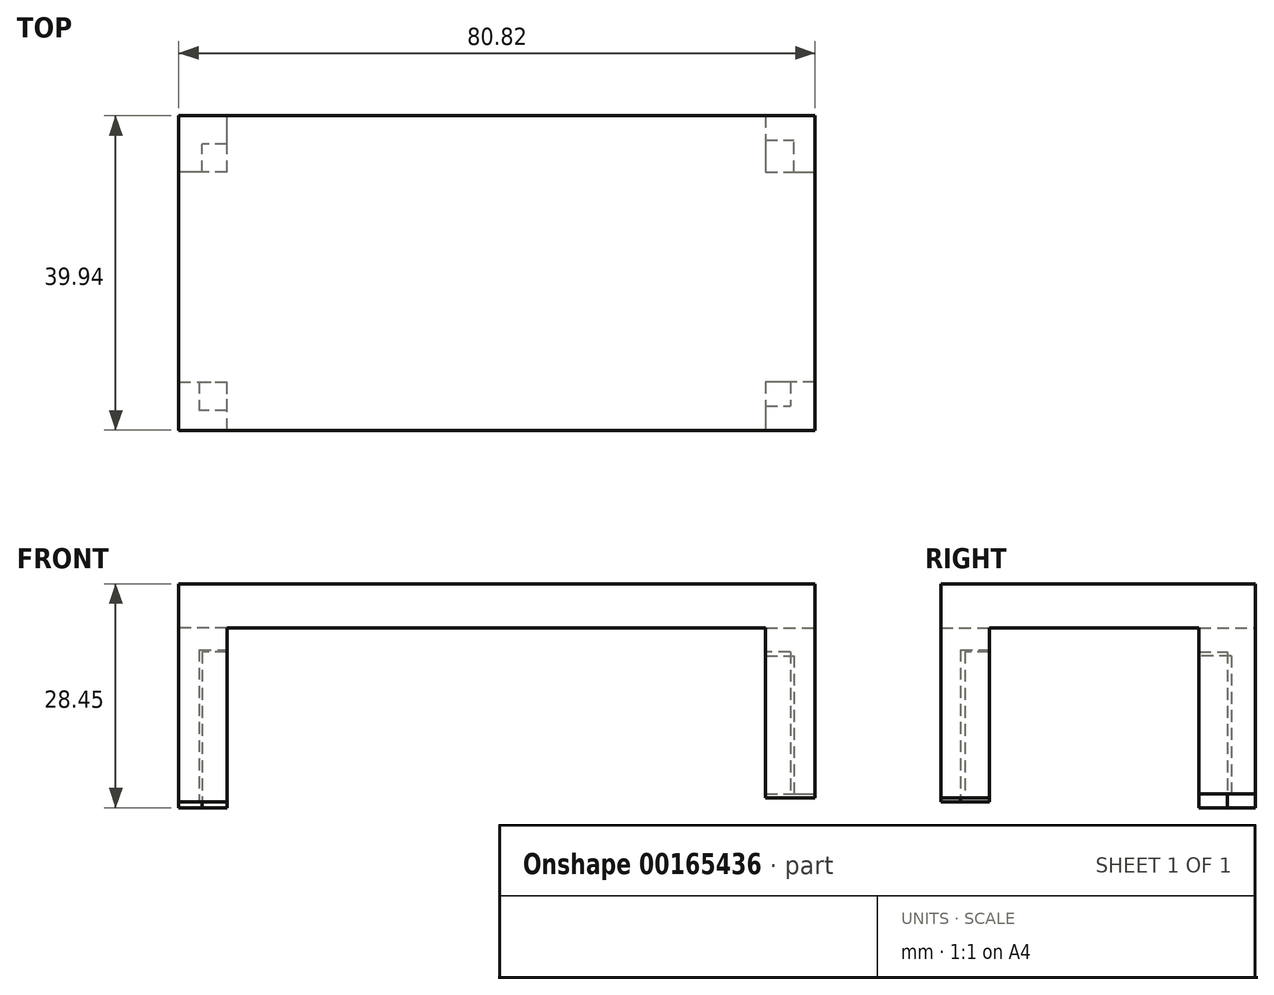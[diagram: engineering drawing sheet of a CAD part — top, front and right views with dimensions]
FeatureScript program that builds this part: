
annotation { "Feature Type Name" : "Feature", "Feature Type Description" : "" }
export const myFeature = defineFeature(function(context is Context, id is Id, definition is map)
    precondition{}
    {
        {
            var Q0;
            Q0=qCreatedBy(makeId("Top.planeOp"),FACE);
            var sketch = newSketch(context, id + "F0", { "sketchPlane" : qUnion([Q0])});
            skLineSegment(sketch, "E0.bottom", {"start": v(-43.18, 17.66) * mm, "end": v(37.64, 17.66) * mm});
            skLineSegment(sketch, "E0.top", {"start": v(-43.18, -22.28) * mm, "end": v(37.64, -22.28) * mm});
            skLineSegment(sketch, "E0.left", {"start": v(-43.18, 17.66) * mm, "end": v(-43.18, -22.28) * mm});
            skLineSegment(sketch, "E0.right", {"start": v(37.64, 17.66) * mm, "end": v(37.64, -22.28) * mm});
            skSolve(sketch);
        }
        {
            var Q0;
            Q0=makeQuery(id+"F0.imprint","IMPRINT",FACE,{"disambiguationData":[TD([[makeQuery(id+"F0.imprint","IMPRINT",EDGE,{"derivedFrom":sQuery(id+"F0.wireOp",EDGE,"E0.bottom")}),-1.0]])]});
            extrude(context, id + "F1", {"entities" : qUnion([Q0]), "depth" : 5.6 * mm});
        }
        {
            var Q0;
            Q0=makeQuery(id+"F1.opExtrude","CAP_FACE",FACE,{"disambiguationData":[OSD([sQuery(id+"F0.wireOp",EDGE,"E0.bottom"),sQuery(id+"F0.wireOp",EDGE,"E0.top"),sQuery(id+"F0.wireOp",EDGE,"E0.left"),sQuery(id+"F0.wireOp",EDGE,"E0.right")])],"isStart":true});
            var sketch = newSketch(context, id + "F2", { "sketchPlane" : qUnion([Q0])});
            skLineSegment(sketch, "E1.bottom", {"start": v(-43.18, 22.28) * mm, "end": v(-37.04, 22.28) * mm});
            skLineSegment(sketch, "E1.top", {"start": v(-43.18, 16.14) * mm, "end": v(-37.04, 16.14) * mm});
            skLineSegment(sketch, "E1.left", {"start": v(-43.18, 22.28) * mm, "end": v(-43.18, 16.14) * mm});
            skLineSegment(sketch, "E1.right", {"start": v(-37.04, 22.28) * mm, "end": v(-37.04, 16.14) * mm});
            skLineSegment(sketch, "E2.bottom", {"start": v(37.64, 16.14) * mm, "end": v(31.35, 16.14) * mm});
            skLineSegment(sketch, "E2.top", {"start": v(37.64, 22.28) * mm, "end": v(31.35, 22.28) * mm});
            skLineSegment(sketch, "E2.left", {"start": v(37.64, 16.14) * mm, "end": v(37.64, 22.28) * mm});
            skLineSegment(sketch, "E2.right", {"start": v(31.35, 16.14) * mm, "end": v(31.35, 22.28) * mm});
            skLineSegment(sketch, "E3.bottom", {"start": v(31.35, -17.66) * mm, "end": v(37.64, -17.66) * mm});
            skLineSegment(sketch, "E3.top", {"start": v(31.35, -10.5) * mm, "end": v(37.64, -10.5) * mm});
            skLineSegment(sketch, "E3.left", {"start": v(31.35, -17.66) * mm, "end": v(31.35, -10.5) * mm});
            skLineSegment(sketch, "E3.right", {"start": v(37.64, -17.66) * mm, "end": v(37.64, -10.5) * mm});
            skLineSegment(sketch, "E4.bottom", {"start": v(-37.04, -10.5) * mm, "end": v(-43.18, -10.5) * mm});
            skLineSegment(sketch, "E4.top", {"start": v(-37.04, -17.66) * mm, "end": v(-43.18, -17.66) * mm});
            skLineSegment(sketch, "E4.left", {"start": v(-37.04, -10.5) * mm, "end": v(-37.04, -17.66) * mm});
            skLineSegment(sketch, "E4.right", {"start": v(-43.18, -10.5) * mm, "end": v(-43.18, -17.66) * mm});
            skSolve(sketch);
        }
        {
            var Q0;
            Q0=makeQuery(id+"F2.imprint","IMPRINT",FACE,{"disambiguationData":[TD([[makeQuery(id+"F2.imprint","IMPRINT",EDGE,{"derivedFrom":sQuery(id+"F2.wireOp",EDGE,"E1.bottom")}),-1.0]])]});
            extrude(context, id + "F3", {"entities" : qUnion([Q0]), "operationType" : NewBodyOperationType.ADD, "depth" : 22.1 * mm});
        }
        {
            var Q0;
            Q0=makeQuery(id+"F2.imprint","IMPRINT",FACE,{"disambiguationData":[TD([[makeQuery(id+"F2.imprint","IMPRINT",EDGE,{"derivedFrom":sQuery(id+"F2.wireOp",EDGE,"E4.bottom")}),1.0]])]});
            extrude(context, id + "F4", {"entities" : qUnion([Q0]), "operationType" : NewBodyOperationType.ADD, "depth" : 22.86 * mm});
        }
        {
            var Q0;
            Q0=makeQuery(id+"F2.imprint","IMPRINT",FACE,{"disambiguationData":[TD([[makeQuery(id+"F2.imprint","IMPRINT",EDGE,{"derivedFrom":sQuery(id+"F2.wireOp",EDGE,"E2.bottom")}),-1.0]])]});
            extrude(context, id + "F5", {"entities" : qUnion([Q0]), "operationType" : NewBodyOperationType.ADD, "depth" : 21.59 * mm});
        }
        {
            var Q0;
            Q0=makeQuery(id+"F2.imprint","IMPRINT",FACE,{"disambiguationData":[TD([[makeQuery(id+"F2.imprint","IMPRINT",EDGE,{"derivedFrom":sQuery(id+"F2.wireOp",EDGE,"E3.bottom")}),1.0]])]});
            extrude(context, id + "F6", {"entities" : qUnion([Q0]), "operationType" : NewBodyOperationType.ADD, "depth" : 23.1 * mm});
        }
        {
            var Q0;
            Q0=makeQuery(id+"F5.opExtrude","CAP_FACE",FACE,{"disambiguationData":[OSD([sQuery(id+"F2.wireOp",EDGE,"E2.bottom"),sQuery(id+"F2.wireOp",EDGE,"E2.top"),sQuery(id+"F2.wireOp",EDGE,"E2.left"),sQuery(id+"F2.wireOp",EDGE,"E2.right")])],"isStart":false});
            var sketch = newSketch(context, id + "F7", { "sketchPlane" : qUnion([Q0])});
            skPoint(sketch, "E5.oppositeSnap0", {"position": v(34.5, 22.28) * mm});
            skPoint(sketch, "E5.oppositeSnap1", {"position": v(37.64, 19.21) * mm});
            skLineSegment(sketch, "E5.bottom", {"start": v(31.35, 16.14) * mm, "end": v(34.5, 16.14) * mm});
            skLineSegment(sketch, "E5.top", {"start": v(31.35, 19.21) * mm, "end": v(34.5, 19.21) * mm});
            skLineSegment(sketch, "E5.left", {"start": v(31.35, 16.14) * mm, "end": v(31.35, 19.21) * mm});
            skLineSegment(sketch, "E5.right", {"start": v(34.5, 16.14) * mm, "end": v(34.5, 19.21) * mm});
            skSolve(sketch);
        }
        {
            var Q0;
            Q0=makeQuery(id+"F7.imprint","IMPRINT",FACE,{"disambiguationData":[TD([[makeQuery(id+"F7.imprint","IMPRINT",EDGE,{"derivedFrom":sQuery(id+"F7.wireOp",EDGE,"E5.bottom")}),-1.0]])]});
            extrude(context, id + "F8", {"entities" : qUnion([Q0]), "operationType" : NewBodyOperationType.REMOVE, "oppositeDirection" : true, "depth" : 18.54 * mm});
        }
        {
            var Q0;
            Q0=makeQuery(id+"F6.opExtrude","CAP_FACE",FACE,{"disambiguationData":[OSD([sQuery(id+"F2.wireOp",EDGE,"E3.bottom"),sQuery(id+"F2.wireOp",EDGE,"E3.top"),sQuery(id+"F2.wireOp",EDGE,"E3.left"),sQuery(id+"F2.wireOp",EDGE,"E3.right")])],"isStart":false});
            extrude(context, id + "F9", {"entities" : qUnion([Q0]), "operationType" : NewBodyOperationType.ADD, "depth" : 25.4 * mm});
        }
        {
            var Q0;
            Q0=makeQuery(id+"F9.opExtrude","CAP_FACE",FACE,{"disambiguationData":[OSD([sQuery(id+"F2.wireOp",EDGE,"E3.bottom"),sQuery(id+"F2.wireOp",EDGE,"E3.top"),sQuery(id+"F2.wireOp",EDGE,"E3.left"),sQuery(id+"F2.wireOp",EDGE,"E3.right")])],"isStart":false});
            var sketch = newSketch(context, id + "F10", { "sketchPlane" : qUnion([Q0])});
            skLineSegment(sketch, "E6.bottom", {"start": v(31.35, -10.5) * mm, "end": v(34.95, -10.5) * mm});
            skLineSegment(sketch, "E6.top", {"start": v(31.35, -14.6) * mm, "end": v(34.95, -14.6) * mm});
            skLineSegment(sketch, "E6.left", {"start": v(31.35, -10.5) * mm, "end": v(31.35, -14.6) * mm});
            skLineSegment(sketch, "E6.right", {"start": v(34.95, -10.5) * mm, "end": v(34.95, -14.6) * mm});
            skSolve(sketch);
        }
        {
            var Q0;
            Q0=makeQuery(id+"F3.opExtrude","CAP_FACE",FACE,{"disambiguationData":[OSD([sQuery(id+"F2.wireOp",EDGE,"E1.bottom"),sQuery(id+"F2.wireOp",EDGE,"E1.top"),sQuery(id+"F2.wireOp",EDGE,"E1.left"),sQuery(id+"F2.wireOp",EDGE,"E1.right")])],"isStart":false});
            var sketch = newSketch(context, id + "F11", { "sketchPlane" : qUnion([Q0])});
            skLineSegment(sketch, "E7.bottom", {"start": v(-37.04, 16.14) * mm, "end": v(-40.57, 16.14) * mm});
            skLineSegment(sketch, "E7.top", {"start": v(-37.04, 19.8) * mm, "end": v(-40.57, 19.8) * mm});
            skLineSegment(sketch, "E7.left", {"start": v(-37.04, 16.14) * mm, "end": v(-37.04, 19.8) * mm});
            skLineSegment(sketch, "E7.right", {"start": v(-40.57, 16.14) * mm, "end": v(-40.57, 19.8) * mm});
            skSolve(sketch);
        }
        {
            var Q0;
            Q0=makeQuery(id+"F4.opExtrude","CAP_FACE",FACE,{"disambiguationData":[OSD([sQuery(id+"F2.wireOp",EDGE,"E4.bottom"),sQuery(id+"F2.wireOp",EDGE,"E4.top"),sQuery(id+"F2.wireOp",EDGE,"E4.left"),sQuery(id+"F2.wireOp",EDGE,"E4.right")])],"isStart":false});
            var sketch = newSketch(context, id + "F12", { "sketchPlane" : qUnion([Q0])});
            skPoint(sketch, "E8.oppositeSnap0", {"position": v(-37.04, -14.08) * mm});
            skLineSegment(sketch, "E8.bottom", {"start": v(-37.04, -10.5) * mm, "end": v(-40.23, -10.5) * mm});
            skLineSegment(sketch, "E8.top", {"start": v(-37.04, -14.08) * mm, "end": v(-40.23, -14.08) * mm});
            skLineSegment(sketch, "E8.left", {"start": v(-37.04, -10.5) * mm, "end": v(-37.04, -14.08) * mm});
            skLineSegment(sketch, "E8.right", {"start": v(-40.23, -10.5) * mm, "end": v(-40.23, -14.08) * mm});
            skSolve(sketch);
        }
        {
            var Q0;
            Q0=makeQuery(id+"F11.imprint","IMPRINT",FACE,{"disambiguationData":[TD([[makeQuery(id+"F11.imprint","IMPRINT",EDGE,{"derivedFrom":sQuery(id+"F11.wireOp",EDGE,"E7.bottom")}),1.0]])]});
            extrude(context, id + "F13", {"entities" : qUnion([Q0]), "operationType" : NewBodyOperationType.REMOVE, "oppositeDirection" : true, "depth" : 19.3 * mm});
        }
        {
            var Q0;
            {var subQ4=sQuery(id+"F10.wireOp",EDGE,"E6.top");Q0=makeQuery(id+"F10.imprint","IMPRINT",FACE,{"disambiguationData":[TD([[makeQuery(id+"F10.imprint","IMPRINT",EDGE,{"derivedFrom":subQ4}),-1.0]])]});}
            extrude(context, id + "F14", {"entities" : qUnion([Q0]), "operationType" : NewBodyOperationType.REMOVE, "oppositeDirection" : true, "depth" : 27.43 * mm});
        }
        {
            var Q0;
            Q0=makeQuery(id+"F9.opExtrude","CAP_FACE",FACE,{"disambiguationData":[OSD([sQuery(id+"F2.wireOp",EDGE,"E3.bottom"),sQuery(id+"F2.wireOp",EDGE,"E3.top"),sQuery(id+"F2.wireOp",EDGE,"E3.left"),sQuery(id+"F2.wireOp",EDGE,"E3.right")])],"isStart":false});
            extrude(context, id + "F15", {"entities" : qUnion([Q0]), "operationType" : NewBodyOperationType.REMOVE, "oppositeDirection" : true, "depth" : 44.96 * mm});
        }
        {
            var Q0;
            Q0=makeQuery(id+"F12.imprint","IMPRINT",FACE,{"disambiguationData":[TD([[makeQuery(id+"F12.imprint","IMPRINT",EDGE,{"derivedFrom":sQuery(id+"F12.wireOp",EDGE,"E8.bottom")}),1.0]])]});
            extrude(context, id + "F16", {"entities" : qUnion([Q0]), "operationType" : NewBodyOperationType.REMOVE, "oppositeDirection" : true, "depth" : 19.8 * mm});
        }
    });
